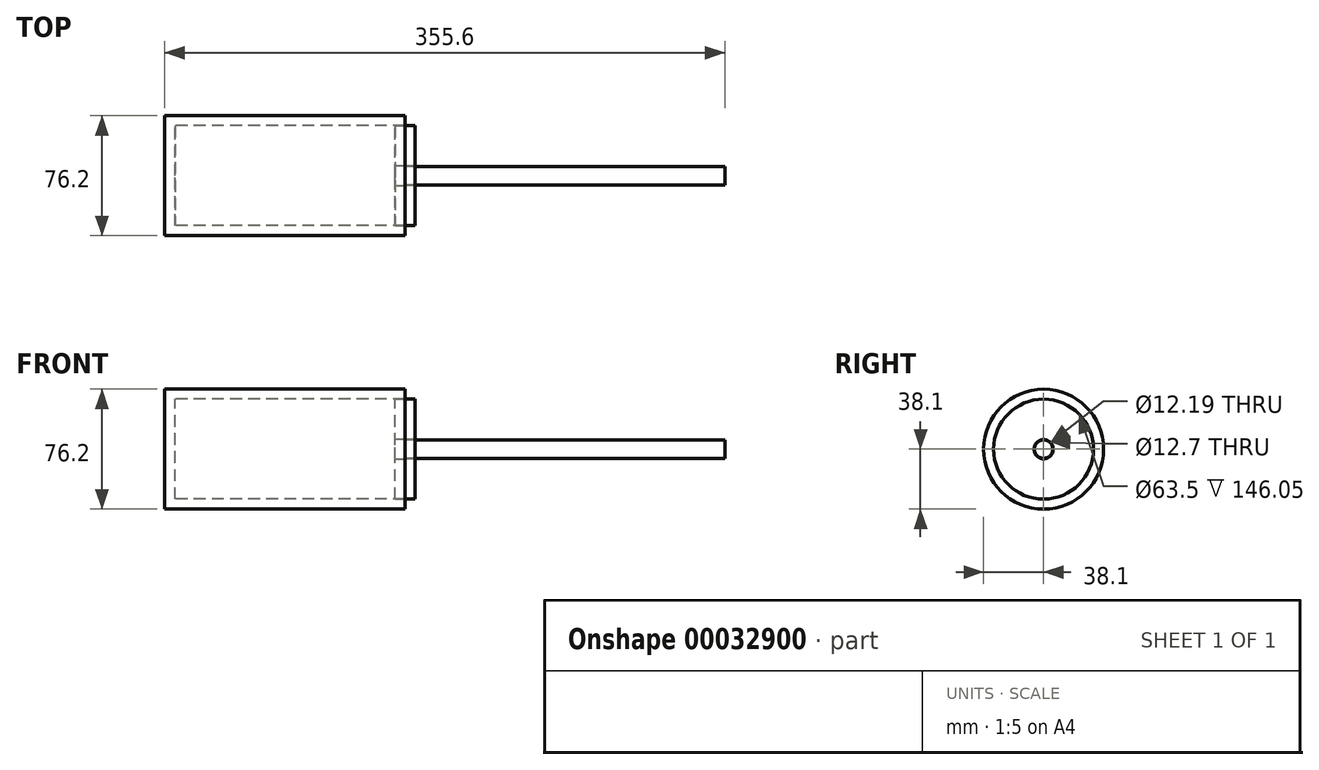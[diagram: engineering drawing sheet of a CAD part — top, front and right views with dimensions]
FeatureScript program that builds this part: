
annotation { "Feature Type Name" : "Feature", "Feature Type Description" : "" }
export const myFeature = defineFeature(function(context is Context, id is Id, definition is map)
    precondition{}
    {
        {
            var Q0;
            Q0=qCreatedBy(makeId("Right.planeOp"),FACE);
            var sketch = newSketch(context, id + "F0", { "sketchPlane" : qUnion([Q0])});
            skCircle(sketch, "E0", {"center": v(0, 0) * mm, "radius": 38.1 * mm});
            skSolve(sketch);
        }
        {
            var Q0;
            Q0=makeQuery(id+"F0.imprint","IMPRINT",FACE,{"disambiguationData":[TD([[makeQuery(id+"F0.imprint","IMPRINT",EDGE,{"derivedFrom":sQuery(id+"F0.wireOp",EDGE,"E0")}),1.0]])]});
            extrude(context, id + "F1", {"entities" : qUnion([Q0]), "endBound" : BoundingType.SYMMETRIC, "depth" : 152.4 * mm});
        }
        {
            var Q0;
            Q0=makeQuery(id+"F1.opExtrude","CAP_FACE",FACE,{"disambiguationData":[OSD([sQuery(id+"F0.wireOp",EDGE,"E0")])],"isStart":false});
            shell(context, id + "F2", {"entities" : qUnion([Q0]), "thickness" : 6.35 * mm});
        }
        {
            var Q0;
            Q0=makeQuery(id+"F1.opExtrude","CAP_FACE",FACE,{"disambiguationData":[OSD([sQuery(id+"F0.wireOp",EDGE,"E0")])],"isStart":false});
            var sketch = newSketch(context, id + "F3", { "sketchPlane" : qUnion([Q0])});
            skCircle(sketch, "E1", {"center": v(0, 0) * mm, "radius": 31.75 * mm});
            skSolve(sketch);
        }
        {
            var Q0;
            Q0=makeQuery(id+"F3.imprint","IMPRINT",FACE,{"disambiguationData":[TD([[makeQuery(id+"F3.imprint","IMPRINT",EDGE,{"derivedFrom":sQuery(id+"F3.wireOp",EDGE,"E1")}),1.0]])]});
            var sketch = newSketch(context, id + "F4", { "sketchPlane" : qUnion([Q0])});
            skCircle(sketch, "E2", {"center": v(0, 0) * mm, "radius": 5.84 * mm});
            skSolve(sketch);
        }
        {
            var Q0;
            Q0 = qSketchRegion(id + "F4", true);
            extrude(context, id + "F5", {"entities" : qUnion([Q0]), "depth" : 203.2 * mm});
        }
        {
            var Q0;
            Q0=makeQuery(id+"F3.imprint","IMPRINT",FACE,{"disambiguationData":[TD([[makeQuery(id+"F3.imprint","IMPRINT",EDGE,{"derivedFrom":sQuery(id+"F3.wireOp",EDGE,"E1")}),1.0]])]});
            var sketch = newSketch(context, id + "F6", { "sketchPlane" : qUnion([Q0])});
            skCircle(sketch, "E3", {"center": v(0, 0) * mm, "radius": 31.75 * mm});
            skSolve(sketch);
        }
        {
            var Q0;
            Q0 = qSketchRegion(id + "F6", true);
            extrude(context, id + "F7", {"entities" : qUnion([Q0]), "depth" : 6.35 * mm});
        }
        {
            var Q0;
            Q0 = qSketchRegion(id + "F3", true);
            extrude(context, id + "F8", {"entities" : qUnion([Q0]), "oppositeDirection" : true, "depth" : 6.35 * mm});
        }
        {
            var Q0;
            Q0=sQuery(id+"F3.wireOp",VERTEX,"E1.center");
            var Q1;
            Q1=makeQuery(id+"F8.opExtrude","SWEPT_BODY",BODY,{"disambiguationData":[OSD([sQuery(id+"F3.wireOp",EDGE,"E1")])]});
            hole(context, id + "F9", {"style" : HoleStyle.SIMPLE, "holeDiameter" : 12.7 * mm, "endStyle" : HoleEndStyle.THROUGH, "locations" : qUnion([Q0]), "scope" : qUnion([Q1])});
        }
        {
            var Q0;
            Q0=sQuery(id+"F3.wireOp",VERTEX,"E1.center");
            var Q1;
            Q1=makeQuery(id+"F7.opExtrude","SWEPT_BODY",BODY,{"disambiguationData":[OSD([sQuery(id+"F6.wireOp",EDGE,"E3")])]});
            hole(context, id + "F10", {"style" : HoleStyle.SIMPLE, "holeDiameter" : 12.2 * mm, "endStyle" : HoleEndStyle.THROUGH, "oppositeDirection" : true, "locations" : qUnion([Q0]), "scope" : qUnion([Q1])});
        }
    });
